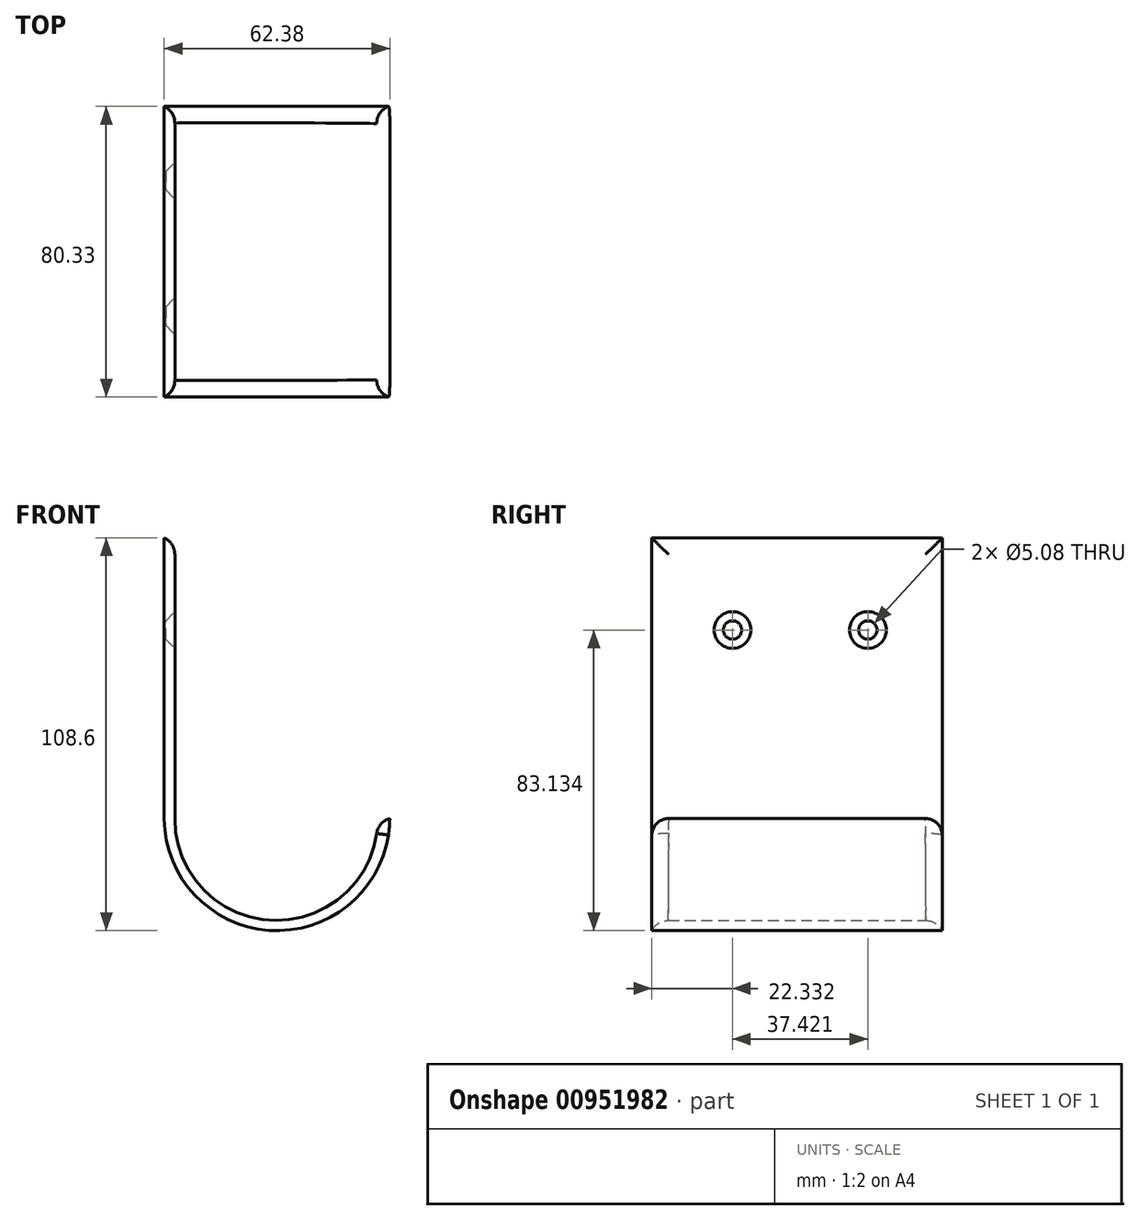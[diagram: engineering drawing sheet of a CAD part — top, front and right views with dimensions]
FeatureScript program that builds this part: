
annotation { "Feature Type Name" : "Feature", "Feature Type Description" : "" }
export const myFeature = defineFeature(function(context is Context, id is Id, definition is map)
    precondition{}
    {
        {
            var Q0;
            Q0=qCreatedBy(makeId("Front.planeOp"),FACE);
            var sketch = newSketch(context, id + "F0", { "sketchPlane" : qUnion([Q0])});
            skLineSegment(sketch, "E0", {"start": v(-47.64, 53.48) * mm, "end": v(-47.64, -23.93) * mm});
            skLineSegment(sketch, "E1", {"start": v(-47.64, 53.48) * mm, "end": v(-44.7, 53.48) * mm});
            skLineSegment(sketch, "E2", {"start": v(-44.7, 53.48) * mm, "end": v(-44.7, -24.28) * mm});
            skArc(sketch, "E3", {"start": v(-44.7, -24.28) * mm, "mid": v(-16.45, -52.33) * mm, "end": v(11.4, -23.9) * mm});
            skArc(sketch, "E4", {"start": v(-47.64, -23.93) * mm, "mid": v(-16.44, -55.12) * mm, "end": v(14.74, -23.9) * mm});
            skLineSegment(sketch, "E5", {"start": v(11.4, -23.9) * mm, "end": v(14.74, -23.9) * mm});
            skSolve(sketch);
        }
        {
            var Q0;
            Q0=makeQuery(id+"F0.imprint","IMPRINT",FACE,{"disambiguationData":[TD([[makeQuery(id+"F0.imprint","IMPRINT",EDGE,{"derivedFrom":sQuery(id+"F0.wireOp",EDGE,"E0")}),1.0]])]});
            extrude(context, id + "F1", {"entities" : qUnion([Q0]), "depth" : 80.33 * mm, "offsetDistance" : 25.4 * mm});
        }
        {
            var Q0;
            Q0=makeQuery(id+"F1.opExtrude","CAP_EDGE",EDGE,{"disambiguationData":[OSD([sQuery(id+"F0.wireOp",EDGE,"E2")])],"isStart":false});
            var Q1;
            Q1=makeQuery(id+"F1.opExtrude","SWEPT_EDGE",EDGE,{"disambiguationData":[OSD([sQuery(id+"F0.wireOp",EDGE,"E1"),sQuery(id+"F0.wireOp",EDGE,"E2")])]});
            var Q2;
            Q2=makeQuery(id+"F1.opExtrude","CAP_EDGE",EDGE,{"disambiguationData":[OSD([sQuery(id+"F0.wireOp",EDGE,"E2")])],"isStart":true});
            var Q3;
            Q3=makeQuery(id+"F1.opExtrude","CAP_EDGE",EDGE,{"disambiguationData":[OSD([sQuery(id+"F0.wireOp",EDGE,"E3")])],"isStart":true});
            var Q4;
            Q4=makeQuery(id+"F1.opExtrude","CAP_EDGE",EDGE,{"disambiguationData":[OSD([sQuery(id+"F0.wireOp",EDGE,"E3")])],"isStart":false});
            fillet(context, id + "F2", {"entities" : qUnion([Q0, Q1, Q2, Q3, Q4]), "radius" : 5.08 * mm, "tangentPropagation" : true, "allowEdgeOverflow" : false});
        }
        {
            var Q0;
            Q0=makeQuery(id+"F1.opExtrude","SWEPT_EDGE",EDGE,{"disambiguationData":[OSD([sQuery(id+"F0.wireOp",EDGE,"E3"),sQuery(id+"F0.wireOp",EDGE,"E5")])]});
            fillet(context, id + "F3", {"entities" : qUnion([Q0]), "radius" : 5.08 * mm, "tangentPropagation" : true, "allowEdgeOverflow" : false});
        }
        {
            var Q0;
            Q0=makeQuery(id+"F1.opExtrude","SWEPT_FACE",FACE,{"disambiguationData":[OSD([sQuery(id+"F0.wireOp",EDGE,"E2")])]});
            var sketch = newSketch(context, id + "F4", { "sketchPlane" : qUnion([Q0])});
            skLineSegment(sketch, "E6", {"start": v(-58, 28.01) * mm, "end": v(-20.58, 28.01) * mm});
            skSolve(sketch);
        }
        {
            var Q0;
            Q0=sQuery(id+"F4.wireOp",VERTEX,"E6.start");
            var Q1;
            Q1=sQuery(id+"F4.wireOp",VERTEX,"E6.end");
            var Q2;
            Q2=makeQuery(id+"F1.opExtrude","SWEPT_BODY",BODY,{"disambiguationData":[OSD([sQuery(id+"F0.wireOp",EDGE,"E0"),sQuery(id+"F0.wireOp",EDGE,"E1"),sQuery(id+"F0.wireOp",EDGE,"E2"),sQuery(id+"F0.wireOp",EDGE,"E3"),sQuery(id+"F0.wireOp",EDGE,"E4"),sQuery(id+"F0.wireOp",EDGE,"E5")])]});
            hole(context, id + "F5", {"style" : HoleStyle.C_SINK, "endStyle" : HoleEndStyle.THROUGH, "holeDiameter" : 5.08 * mm, "cSinkDiameter" : 10.16 * mm, "cSinkAngle" : 90 * degree, "majorDiameter" : 6.35 * mm, "isTappedThrough" : true, "tappedDepth" : 12.7 * mm, "tapClearance" : 3, "locations" : qUnion([Q0, Q1]), "scope" : qUnion([Q2])});
        }
    });
